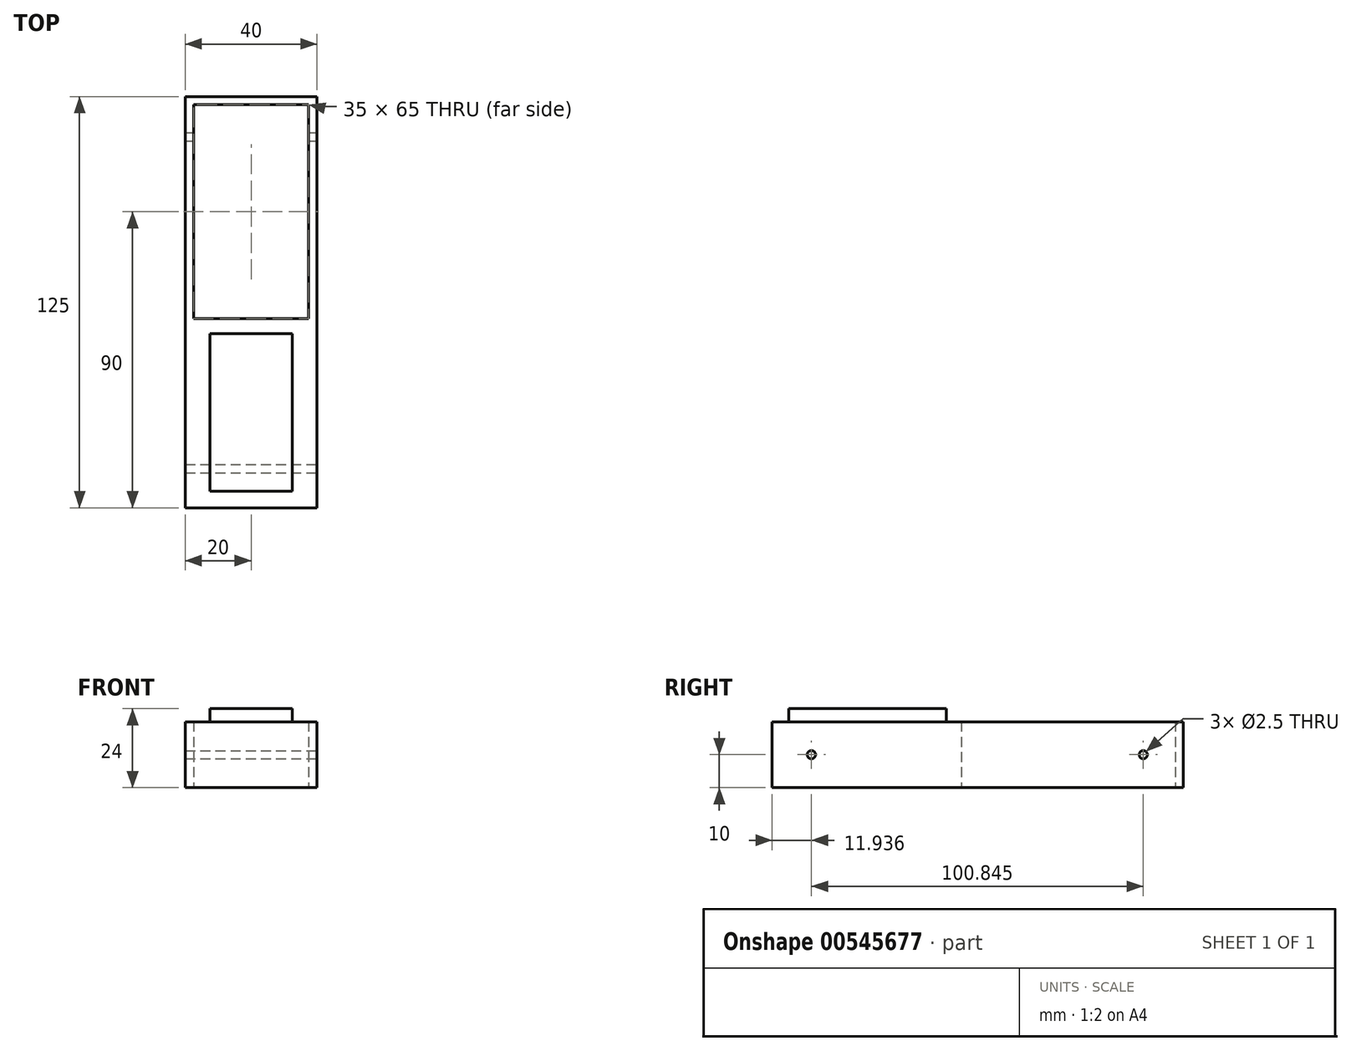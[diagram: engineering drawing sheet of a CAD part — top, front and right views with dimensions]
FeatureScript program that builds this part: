
annotation { "Feature Type Name" : "Feature", "Feature Type Description" : "" }
export const myFeature = defineFeature(function(context is Context, id is Id, definition is map)
    precondition{}
    {
        {
            var Q0;
            Q0=qCreatedBy(makeId("Top.planeOp"),FACE);
            var sketch = newSketch(context, id + "F0", { "sketchPlane" : qUnion([Q0])});
            skLineSegment(sketch, "E0.bottom", {"start": v(20, -62.5) * mm, "end": v(-20, -62.5) * mm});
            skLineSegment(sketch, "E0.top", {"start": v(20, 62.5) * mm, "end": v(-20, 62.5) * mm});
            skLineSegment(sketch, "E0.left", {"start": v(20, -62.5) * mm, "end": v(20, 62.5) * mm});
            skLineSegment(sketch, "E0.right", {"start": v(-20, -62.5) * mm, "end": v(-20, 62.5) * mm});
            skPoint(sketch, "E0.middle", {"position": v(0, 0) * mm});
            skSolve(sketch);
        }
        {
            var Q0;
            Q0=makeQuery(id+"F0.imprint","IMPRINT",FACE,{"disambiguationData":[TD([[makeQuery(id+"F0.imprint","IMPRINT",EDGE,{"derivedFrom":sQuery(id+"F0.wireOp",EDGE,"E0.bottom")}),-1.0]])]});
            extrude(context, id + "F1", {"entities" : qUnion([Q0]), "depth" : 20 * mm, "offsetDistance" : 25 * mm});
        }
        {
            var Q0;
            Q0=makeQuery(id+"F1.opExtrude","CAP_FACE",FACE,{"disambiguationData":[OSD([sQuery(id+"F0.wireOp",EDGE,"E0.bottom"),sQuery(id+"F0.wireOp",EDGE,"E0.top"),sQuery(id+"F0.wireOp",EDGE,"E0.left"),sQuery(id+"F0.wireOp",EDGE,"E0.right")])],"isStart":true});
            var sketch = newSketch(context, id + "F2", { "sketchPlane" : qUnion([Q0])});
            skLineSegment(sketch, "E1.bottom", {"start": v(-17.5, 5) * mm, "end": v(17.5, 5) * mm});
            skLineSegment(sketch, "E1.top", {"start": v(-17.5, -60) * mm, "end": v(17.5, -60) * mm});
            skLineSegment(sketch, "E1.left", {"start": v(-17.5, 5) * mm, "end": v(-17.5, -60) * mm});
            skLineSegment(sketch, "E1.right", {"start": v(17.5, 5) * mm, "end": v(17.5, -60) * mm});
            skSolve(sketch);
        }
        {
            var Q0;
            Q0=makeQuery(id+"F2.imprint","IMPRINT",FACE,{"disambiguationData":[TD([[makeQuery(id+"F2.imprint","IMPRINT",EDGE,{"derivedFrom":sQuery(id+"F2.wireOp",EDGE,"E1.bottom")}),-1.0]])]});
            extrude(context, id + "F3", {"entities" : qUnion([Q0]), "operationType" : NewBodyOperationType.REMOVE, "oppositeDirection" : true, "depth" : 42.6 * mm, "offsetDistance" : 25 * mm});
        }
        {
            var Q0;
            Q0=makeQuery(id+"F1.opExtrude","SWEPT_FACE",FACE,{"disambiguationData":[OSD([sQuery(id+"F0.wireOp",EDGE,"E0.left")])]});
            var sketch = newSketch(context, id + "F4", { "sketchPlane" : qUnion([Q0])});
            skCircle(sketch, "E2", {"center": v(-50.56, 10) * mm, "radius": 1.25 * mm});
            skPoint(sketch, "E2.centerSnap0", {"position": v(-62.5, 10) * mm});
            skSolve(sketch);
        }
        {
            var Q0;
            Q0=makeQuery(id+"F1.opExtrude","CAP_FACE",FACE,{"disambiguationData":[OSD([sQuery(id+"F0.wireOp",EDGE,"E0.bottom"),sQuery(id+"F0.wireOp",EDGE,"E0.top"),sQuery(id+"F0.wireOp",EDGE,"E0.left"),sQuery(id+"F0.wireOp",EDGE,"E0.right")])],"isStart":false});
            var sketch = newSketch(context, id + "F5", { "sketchPlane" : qUnion([Q0])});
            skLineSegment(sketch, "E3.bottom", {"start": v(12.5, -57.5) * mm, "end": v(-12.5, -57.5) * mm});
            skLineSegment(sketch, "E3.top", {"start": v(12.5, -9.5) * mm, "end": v(-12.5, -9.5) * mm});
            skLineSegment(sketch, "E3.left", {"start": v(12.5, -57.5) * mm, "end": v(12.5, -9.5) * mm});
            skLineSegment(sketch, "E3.right", {"start": v(-12.5, -57.5) * mm, "end": v(-12.5, -9.5) * mm});
            skPoint(sketch, "E3.middle", {"position": v(0, -33.5) * mm});
            skSolve(sketch);
        }
        {
            var Q0;
            Q0=makeQuery(id+"F5.imprint","IMPRINT",FACE,{"disambiguationData":[TD([[makeQuery(id+"F5.imprint","IMPRINT",EDGE,{"derivedFrom":sQuery(id+"F5.wireOp",EDGE,"E3.bottom")}),-1.0]])]});
            extrude(context, id + "F6", {"entities" : qUnion([Q0]), "operationType" : NewBodyOperationType.ADD, "depth" : 4 * mm, "offsetDistance" : 25 * mm});
        }
        {
            var Q0;
            Q0 = qSketchRegion(id + "F4", true);
            extrude(context, id + "F7", {"entities" : qUnion([Q0]), "operationType" : NewBodyOperationType.REMOVE, "oppositeDirection" : true, "depth" : 180 * mm, "offsetDistance" : 25 * mm});
        }
        {
            var Q0;
            Q0=makeQuery(id+"F1.opExtrude","SWEPT_FACE",FACE,{"disambiguationData":[OSD([sQuery(id+"F0.wireOp",EDGE,"E0.left")])]});
            var sketch = newSketch(context, id + "F8", { "sketchPlane" : qUnion([Q0])});
            skCircle(sketch, "E4", {"center": v(50.28, 10) * mm, "radius": 1.25 * mm});
            skPoint(sketch, "E4.centerSnap0", {"position": v(62.5, 10) * mm});
            skSolve(sketch);
        }
        {
            var Q0;
            Q0 = qSketchRegion(id + "F8", true);
            extrude(context, id + "F9", {"entities" : qUnion([Q0]), "operationType" : NewBodyOperationType.REMOVE, "oppositeDirection" : true, "depth" : 71 * mm, "offsetDistance" : 25 * mm});
        }
    });
